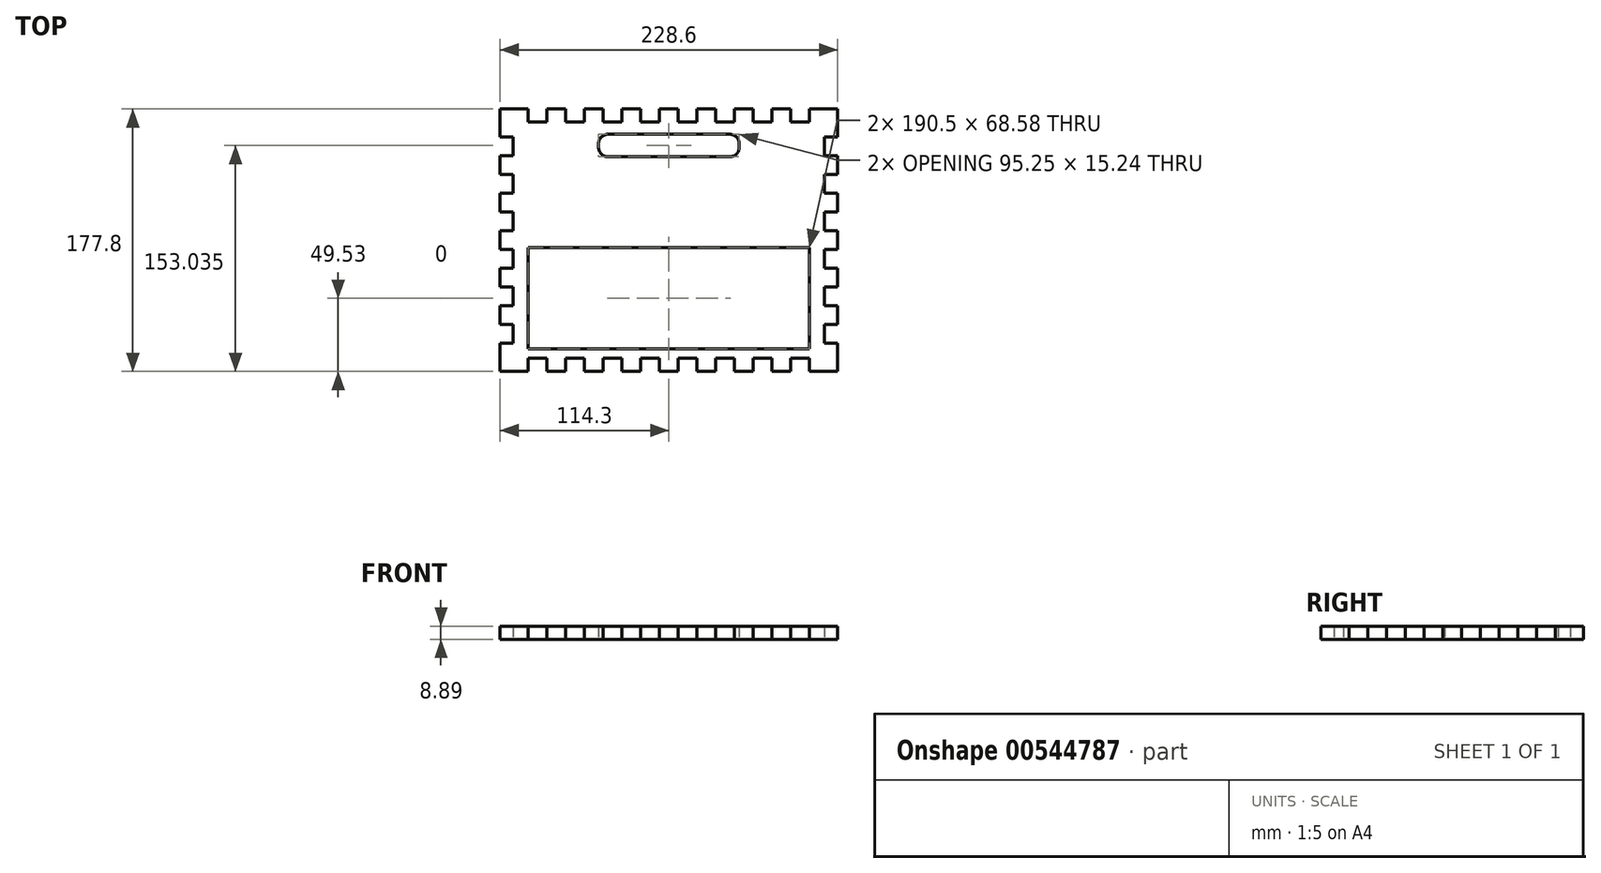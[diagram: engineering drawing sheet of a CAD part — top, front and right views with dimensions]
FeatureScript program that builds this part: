
annotation { "Feature Type Name" : "Feature", "Feature Type Description" : "" }
export const myFeature = defineFeature(function(context is Context, id is Id, definition is map)
    precondition{}
    {
        {
            var Q0;
            Q0=qCreatedBy(makeId("Top.planeOp"),FACE);
            var sketch = newSketch(context, id + "F0", { "sketchPlane" : qUnion([Q0])});
            skLineSegment(sketch, "E0.bottom", {"start": v(0, 0) * mm, "end": v(19.05, 0) * mm});
            skLineSegment(sketch, "E0.left", {"start": v(0, 0) * mm, "end": v(0, -19.05) * mm});
            skLineSegment(sketch, "E1", {"start": v(19.05, 0) * mm, "end": v(19.05, -8.9) * mm});
            skLineSegment(sketch, "E2", {"start": v(19.05, -8.9) * mm, "end": v(31.75, -8.9) * mm});
            skLineSegment(sketch, "E3", {"start": v(31.75, -8.9) * mm, "end": v(31.75, 0) * mm});
            skLineSegment(sketch, "E4", {"start": v(31.75, 0) * mm, "end": v(44.45, 0) * mm});
            skLineSegment(sketch, "E5", {"start": v(44.45, 0) * mm, "end": v(44.45, -8.9) * mm});
            skLineSegment(sketch, "E6", {"start": v(44.45, -8.9) * mm, "end": v(57.15, -8.9) * mm});
            skLineSegment(sketch, "E7", {"start": v(57.15, -8.9) * mm, "end": v(57.15, 0) * mm});
            skLineSegment(sketch, "E8", {"start": v(57.15, 0) * mm, "end": v(69.85, 0) * mm});
            skLineSegment(sketch, "E9", {"start": v(69.85, 0) * mm, "end": v(69.85, -8.9) * mm});
            skLineSegment(sketch, "E10", {"start": v(69.85, -8.9) * mm, "end": v(82.55, -8.9) * mm});
            skLineSegment(sketch, "E11", {"start": v(82.55, -8.9) * mm, "end": v(82.55, 0) * mm});
            skLineSegment(sketch, "E12", {"start": v(82.55, 0) * mm, "end": v(95.25, 0) * mm});
            skLineSegment(sketch, "E13", {"start": v(95.25, 0) * mm, "end": v(95.25, -8.89) * mm});
            skLineSegment(sketch, "E14", {"start": v(95.25, -8.89) * mm, "end": v(107.95, -8.89) * mm});
            skLineSegment(sketch, "E15", {"start": v(107.95, -8.89) * mm, "end": v(107.95, 0) * mm});
            skLineSegment(sketch, "E16.trimOffspring", {"start": v(107.95, 0) * mm, "end": v(120.65, 0) * mm});
            skLineSegment(sketch, "E17", {"start": v(120.65, 0) * mm, "end": v(120.65, -8.9) * mm});
            skLineSegment(sketch, "E18", {"start": v(120.65, -8.89) * mm, "end": v(133.35, -8.89) * mm});
            skLineSegment(sketch, "E19", {"start": v(133.35, -8.89) * mm, "end": v(133.35, 0) * mm});
            skLineSegment(sketch, "E20", {"start": v(133.35, 0) * mm, "end": v(146.05, 0) * mm});
            skLineSegment(sketch, "E21", {"start": v(146.05, 0) * mm, "end": v(146.05, -8.9) * mm});
            skLineSegment(sketch, "E22", {"start": v(146.05, -8.89) * mm, "end": v(158.75, -8.89) * mm});
            skLineSegment(sketch, "E23", {"start": v(158.75, -8.9) * mm, "end": v(158.75, 0) * mm});
            skLineSegment(sketch, "E24.trimOffspring", {"start": v(158.75, 0) * mm, "end": v(171.45, 0) * mm});
            skLineSegment(sketch, "E25", {"start": v(171.45, 0) * mm, "end": v(171.45, -8.89) * mm});
            skLineSegment(sketch, "E26", {"start": v(171.45, -8.9) * mm, "end": v(184.15, -8.9) * mm});
            skLineSegment(sketch, "E27", {"start": v(184.15, -8.89) * mm, "end": v(184.15, 0) * mm});
            skLineSegment(sketch, "E28", {"start": v(184.15, 0) * mm, "end": v(196.85, 0) * mm});
            skLineSegment(sketch, "E29", {"start": v(196.85, 0) * mm, "end": v(196.85, -8.89) * mm});
            skLineSegment(sketch, "E30", {"start": v(196.85, -8.89) * mm, "end": v(209.55, -8.89) * mm});
            skLineSegment(sketch, "E31", {"start": v(209.55, -8.89) * mm, "end": v(209.55, 0) * mm});
            skLineSegment(sketch, "E32.trimOffspring", {"start": v(209.55, 0) * mm, "end": v(228.6, 0) * mm});
            skLineSegment(sketch, "E33", {"start": v(0, -19.05) * mm, "end": v(8.89, -19.05) * mm});
            skLineSegment(sketch, "E34", {"start": v(8.89, -19.05) * mm, "end": v(8.89, -31.75) * mm});
            skLineSegment(sketch, "E35", {"start": v(8.89, -31.75) * mm, "end": v(0, -31.75) * mm});
            skLineSegment(sketch, "E36", {"start": v(0, -31.75) * mm, "end": v(0, -44.45) * mm});
            skLineSegment(sketch, "E37", {"start": v(0, -44.45) * mm, "end": v(8.89, -44.45) * mm});
            skLineSegment(sketch, "E38", {"start": v(8.9, -44.45) * mm, "end": v(8.9, -57.15) * mm});
            skLineSegment(sketch, "E39", {"start": v(8.9, -57.15) * mm, "end": v(0, -57.15) * mm});
            skLineSegment(sketch, "E40", {"start": v(0, -57.15) * mm, "end": v(0, -69.85) * mm});
            skLineSegment(sketch, "E41", {"start": v(0, -69.85) * mm, "end": v(8.9, -69.85) * mm});
            skLineSegment(sketch, "E42", {"start": v(8.9, -69.85) * mm, "end": v(8.9, -82.55) * mm});
            skLineSegment(sketch, "E43", {"start": v(8.9, -82.55) * mm, "end": v(0, -82.55) * mm});
            skLineSegment(sketch, "E44.trimOffspring", {"start": v(0, -82.55) * mm, "end": v(0, -95.25) * mm});
            skLineSegment(sketch, "E45", {"start": v(0, -95.25) * mm, "end": v(8.9, -95.25) * mm});
            skLineSegment(sketch, "E46", {"start": v(8.9, -95.25) * mm, "end": v(8.9, -107.95) * mm});
            skLineSegment(sketch, "E47", {"start": v(8.9, -107.95) * mm, "end": v(0, -107.95) * mm});
            skLineSegment(sketch, "E48", {"start": v(0, -107.95) * mm, "end": v(0, -120.65) * mm});
            skLineSegment(sketch, "E49", {"start": v(0, -120.65) * mm, "end": v(8.9, -120.65) * mm});
            skLineSegment(sketch, "E50", {"start": v(8.9, -120.65) * mm, "end": v(8.9, -133.35) * mm});
            skLineSegment(sketch, "E51", {"start": v(8.9, -133.35) * mm, "end": v(0, -133.35) * mm});
            skLineSegment(sketch, "E52", {"start": v(0, -133.35) * mm, "end": v(0, -146.05) * mm});
            skLineSegment(sketch, "E53", {"start": v(0, -146.05) * mm, "end": v(8.9, -146.05) * mm});
            skLineSegment(sketch, "E54", {"start": v(8.9, -146.05) * mm, "end": v(8.9, -158.75) * mm});
            skLineSegment(sketch, "E55", {"start": v(8.9, -158.75) * mm, "end": v(0, -158.75) * mm});
            skLineSegment(sketch, "E56.trimOffspring", {"start": v(0, -158.75) * mm, "end": v(0, -177.8) * mm});
            skLineSegment(sketch, "E57", {"start": v(0, -88.9) * mm, "end": v(38.1, -88.9) * mm, "construction": true});
            skLineSegment(sketch, "E58", {"start": v(114.3, 0) * mm, "end": v(114.3, -53.65) * mm, "construction": true});
            skLineSegment(sketch, "E59.MirrorCS", {"start": v(228.6, 0) * mm, "end": v(228.6, -19.05) * mm});
            skLineSegment(sketch, "E60.MirrorCS", {"start": v(228.6, -19.05) * mm, "end": v(219.71, -19.05) * mm});
            skLineSegment(sketch, "E61.MirrorCS", {"start": v(219.71, -19.05) * mm, "end": v(219.71, -31.75) * mm});
            skLineSegment(sketch, "E62.MirrorCS", {"start": v(219.71, -31.75) * mm, "end": v(228.6, -31.75) * mm});
            skLineSegment(sketch, "E63.MirrorCS", {"start": v(228.6, -31.75) * mm, "end": v(228.6, -44.45) * mm});
            skLineSegment(sketch, "E64.MirrorCS", {"start": v(228.6, -44.45) * mm, "end": v(219.71, -44.45) * mm});
            skLineSegment(sketch, "E65.MirrorCS", {"start": v(219.71, -44.45) * mm, "end": v(219.71, -57.15) * mm});
            skLineSegment(sketch, "E66.MirrorCS", {"start": v(219.71, -57.15) * mm, "end": v(228.6, -57.15) * mm});
            skLineSegment(sketch, "E67.MirrorCS", {"start": v(228.6, -57.15) * mm, "end": v(228.6, -69.85) * mm});
            skLineSegment(sketch, "E68.MirrorCS", {"start": v(228.6, -69.85) * mm, "end": v(219.71, -69.85) * mm});
            skLineSegment(sketch, "E69.MirrorCS", {"start": v(219.71, -69.85) * mm, "end": v(219.71, -82.55) * mm});
            skLineSegment(sketch, "E70.MirrorCS", {"start": v(219.71, -82.55) * mm, "end": v(228.6, -82.55) * mm});
            skLineSegment(sketch, "E71.MirrorCS", {"start": v(228.6, -82.55) * mm, "end": v(228.6, -95.25) * mm});
            skLineSegment(sketch, "E72.MirrorCS", {"start": v(228.6, -95.25) * mm, "end": v(219.71, -95.25) * mm});
            skLineSegment(sketch, "E73.MirrorCS", {"start": v(219.71, -95.25) * mm, "end": v(219.71, -107.95) * mm});
            skLineSegment(sketch, "E74.MirrorCS", {"start": v(228.6, -107.95) * mm, "end": v(228.6, -120.65) * mm});
            skLineSegment(sketch, "E75.MirrorCS", {"start": v(228.6, -120.65) * mm, "end": v(219.71, -120.65) * mm});
            skLineSegment(sketch, "E76.MirrorCS", {"start": v(219.71, -120.65) * mm, "end": v(219.71, -133.35) * mm});
            skLineSegment(sketch, "E77.MirrorCS", {"start": v(219.71, -133.35) * mm, "end": v(228.6, -133.35) * mm});
            skLineSegment(sketch, "E78.MirrorCS", {"start": v(228.6, -133.35) * mm, "end": v(228.6, -146.05) * mm});
            skLineSegment(sketch, "E79.MirrorCS", {"start": v(219.71, -107.95) * mm, "end": v(228.6, -107.95) * mm});
            skLineSegment(sketch, "E80.MirrorCS", {"start": v(228.6, -158.75) * mm, "end": v(228.6, -177.8) * mm});
            skLineSegment(sketch, "E81.MirrorCS", {"start": v(219.71, -158.75) * mm, "end": v(228.6, -158.75) * mm});
            skLineSegment(sketch, "E82.MirrorCS", {"start": v(219.71, -146.05) * mm, "end": v(219.71, -158.75) * mm});
            skLineSegment(sketch, "E83.MirrorCS", {"start": v(228.6, -146.05) * mm, "end": v(219.71, -146.05) * mm});
            skLineSegment(sketch, "E84.MirrorCS", {"start": v(0, -177.8) * mm, "end": v(19.05, -177.8) * mm});
            skLineSegment(sketch, "E85.MirrorCS", {"start": v(19.05, -177.8) * mm, "end": v(19.05, -168.9) * mm});
            skLineSegment(sketch, "E86.MirrorCS", {"start": v(19.05, -168.9) * mm, "end": v(31.75, -168.9) * mm});
            skLineSegment(sketch, "E87.MirrorCS", {"start": v(31.75, -168.9) * mm, "end": v(31.75, -177.8) * mm});
            skLineSegment(sketch, "E88.MirrorCS", {"start": v(31.75, -177.8) * mm, "end": v(44.45, -177.8) * mm});
            skLineSegment(sketch, "E89.MirrorCS", {"start": v(44.45, -177.8) * mm, "end": v(44.45, -168.9) * mm});
            skLineSegment(sketch, "E90.MirrorCS", {"start": v(44.45, -168.9) * mm, "end": v(57.15, -168.9) * mm});
            skLineSegment(sketch, "E91.MirrorCS", {"start": v(57.15, -168.9) * mm, "end": v(57.15, -177.8) * mm});
            skLineSegment(sketch, "E92.MirrorCS", {"start": v(57.15, -177.8) * mm, "end": v(69.85, -177.8) * mm});
            skLineSegment(sketch, "E93.MirrorCS", {"start": v(69.85, -177.8) * mm, "end": v(69.85, -168.9) * mm});
            skLineSegment(sketch, "E94.MirrorCS", {"start": v(69.85, -168.9) * mm, "end": v(82.55, -168.9) * mm});
            skLineSegment(sketch, "E95.MirrorCS", {"start": v(82.55, -168.9) * mm, "end": v(82.55, -177.8) * mm});
            skLineSegment(sketch, "E96.MirrorCS", {"start": v(82.55, -177.8) * mm, "end": v(95.25, -177.8) * mm});
            skLineSegment(sketch, "E97.MirrorCS", {"start": v(95.25, -177.8) * mm, "end": v(95.25, -168.9) * mm});
            skLineSegment(sketch, "E98.MirrorCS", {"start": v(95.25, -168.9) * mm, "end": v(107.95, -168.9) * mm});
            skLineSegment(sketch, "E99.MirrorCS", {"start": v(107.95, -168.9) * mm, "end": v(107.95, -177.8) * mm});
            skLineSegment(sketch, "E100.MirrorCS", {"start": v(107.95, -177.8) * mm, "end": v(120.65, -177.8) * mm});
            skLineSegment(sketch, "E101.MirrorCS", {"start": v(120.65, -177.8) * mm, "end": v(120.65, -168.9) * mm});
            skLineSegment(sketch, "E102.MirrorCS", {"start": v(120.65, -168.9) * mm, "end": v(133.35, -168.9) * mm});
            skLineSegment(sketch, "E103.MirrorCS", {"start": v(133.35, -168.9) * mm, "end": v(133.35, -177.8) * mm});
            skLineSegment(sketch, "E104.MirrorCS", {"start": v(133.35, -177.8) * mm, "end": v(146.05, -177.8) * mm});
            skLineSegment(sketch, "E105.MirrorCS", {"start": v(146.05, -177.8) * mm, "end": v(146.05, -168.9) * mm});
            skLineSegment(sketch, "E106.MirrorCS", {"start": v(146.05, -168.9) * mm, "end": v(158.75, -168.9) * mm});
            skLineSegment(sketch, "E107.MirrorCS", {"start": v(158.75, -168.9) * mm, "end": v(158.75, -177.8) * mm});
            skLineSegment(sketch, "E108.MirrorCS", {"start": v(158.75, -177.8) * mm, "end": v(171.45, -177.8) * mm});
            skLineSegment(sketch, "E109.MirrorCS", {"start": v(171.45, -177.8) * mm, "end": v(171.45, -168.9) * mm});
            skLineSegment(sketch, "E110.MirrorCS", {"start": v(171.45, -168.9) * mm, "end": v(184.15, -168.9) * mm});
            skLineSegment(sketch, "E111.MirrorCS", {"start": v(184.15, -168.9) * mm, "end": v(184.15, -177.8) * mm});
            skLineSegment(sketch, "E112.MirrorCS", {"start": v(184.15, -177.8) * mm, "end": v(196.85, -177.8) * mm});
            skLineSegment(sketch, "E113.MirrorCS", {"start": v(196.85, -177.8) * mm, "end": v(196.85, -168.91) * mm});
            skLineSegment(sketch, "E114.MirrorCS", {"start": v(196.85, -168.91) * mm, "end": v(209.55, -168.91) * mm});
            skLineSegment(sketch, "E115.MirrorCS", {"start": v(209.55, -168.91) * mm, "end": v(209.55, -177.8) * mm});
            skLineSegment(sketch, "E116.MirrorCS", {"start": v(209.55, -177.8) * mm, "end": v(228.6, -177.8) * mm});
            skPoint(sketch, "E117.firstSnap0", {"position": v(19.05, -88.9) * mm});
            skLineSegment(sketch, "E117.bottom", {"start": v(19.05, -93.98) * mm, "end": v(209.55, -93.98) * mm});
            skLineSegment(sketch, "E117.top", {"start": v(19.05, -162.56) * mm, "end": v(209.55, -162.56) * mm});
            skLineSegment(sketch, "E117.left", {"start": v(19.05, -93.98) * mm, "end": v(19.05, -162.56) * mm});
            skLineSegment(sketch, "E117.right", {"start": v(209.55, -93.98) * mm, "end": v(209.55, -162.56) * mm});
            skLineSegment(sketch, "E118.bottom", {"start": v(73.02, -17.15) * mm, "end": v(155.57, -17.15) * mm});
            skLineSegment(sketch, "E118.top", {"start": v(73.02, -32.38) * mm, "end": v(155.57, -32.38) * mm});
            skLineSegment(sketch, "E118.left", {"start": v(66.67, -23.5) * mm, "end": v(66.67, -26.04) * mm});
            skLineSegment(sketch, "E118.right", {"start": v(161.92, -23.5) * mm, "end": v(161.92, -26.03) * mm});
            skPoint(sketch, "E119.visualSharp", {"position": v(66.67, -17.15) * mm});
            skArc(sketch, "E119.filletArc", {"start": v(73.02, -17.14) * mm, "mid": v(68.53, -19) * mm, "end": v(66.67, -23.5) * mm});
            skPoint(sketch, "E120.visualSharp", {"position": v(66.67, -32.39) * mm});
            skArc(sketch, "E120.filletArc", {"start": v(66.67, -26.04) * mm, "mid": v(68.53, -30.53) * mm, "end": v(73.02, -32.39) * mm});
            skPoint(sketch, "E121.visualSharp", {"position": v(161.92, -32.38) * mm});
            skArc(sketch, "E121.filletArc", {"start": v(155.57, -32.39) * mm, "mid": v(160.07, -30.53) * mm, "end": v(161.92, -26.03) * mm});
            skPoint(sketch, "E122.visualSharp", {"position": v(161.92, -17.14) * mm});
            skArc(sketch, "E122.filletArc", {"start": v(161.92, -23.5) * mm, "mid": v(160.07, -19) * mm, "end": v(155.57, -17.15) * mm});
            skLineSegment(sketch, "E123", {"start": v(114.3, 0) * mm, "end": v(114.3, -17.15) * mm, "construction": true});
            skSolve(sketch);
        }
        {
            var Q0;
            Q0=makeQuery(id+"F0.imprint","IMPRINT",FACE,{"disambiguationData":[TD([[makeQuery(id+"F0.imprint","IMPRINT",EDGE,{"derivedFrom":sQuery(id+"F0.wireOp",EDGE,"E0.bottom")}),-1.0]])]});
            extrude(context, id + "F1", {"entities" : qUnion([Q0]), "depth" : 8.9 * mm, "offsetDistance" : 25.4 * mm});
        }
        {
            var Q0;
            Q0=makeQuery(id+"F0.imprint","IMPRINT",FACE,{"disambiguationData":[TD([[makeQuery(id+"F0.imprint","IMPRINT",EDGE,{"derivedFrom":sQuery(id+"F0.wireOp",EDGE,"E38")}),1.0]])]});
            extrude(context, id + "F2", {"entities" : qUnion([Q0]), "depth" : 8.9 * mm, "offsetDistance" : 25.4 * mm});
        }
    });
